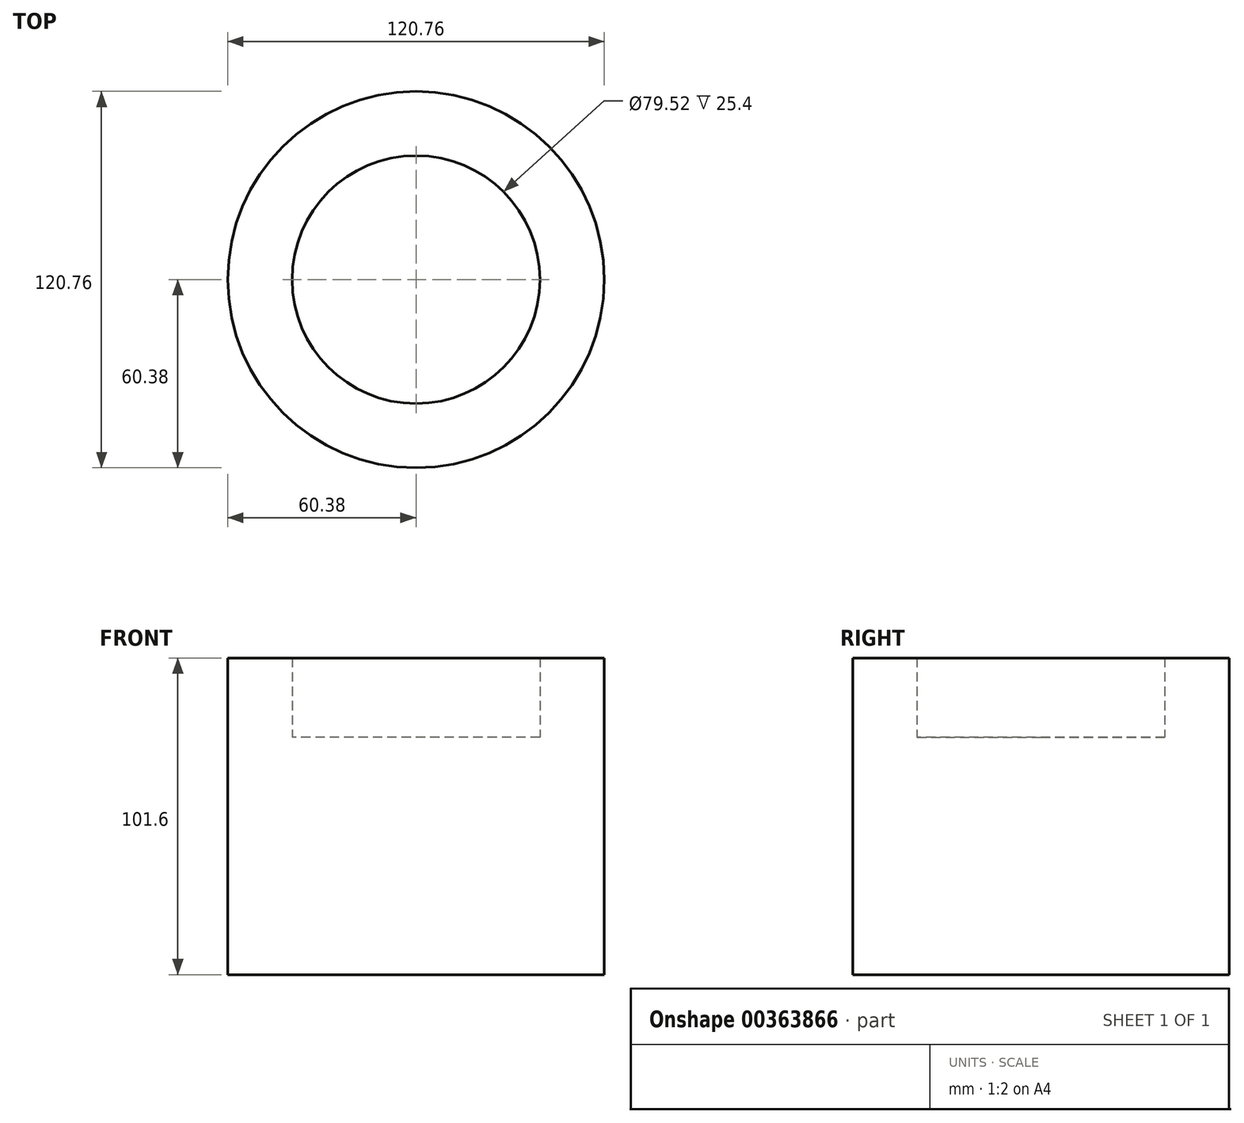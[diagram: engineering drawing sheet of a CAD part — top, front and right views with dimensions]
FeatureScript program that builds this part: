
annotation { "Feature Type Name" : "Feature", "Feature Type Description" : "" }
export const myFeature = defineFeature(function(context is Context, id is Id, definition is map)
    precondition{}
    {
        {
            var Q0;
            Q0=qCreatedBy(makeId("Top.planeOp"),FACE);
            var sketch = newSketch(context, id + "F0", { "sketchPlane" : qUnion([Q0])});
            skCircle(sketch, "E0", {"center": v(0, 0) * mm, "radius": 60.38 * mm});
            skSolve(sketch);
        }
        {
            var Q0;
            Q0=makeQuery(id+"F0.imprint","IMPRINT",FACE,{"disambiguationData":[TD([[makeQuery(id+"F0.imprint","IMPRINT",EDGE,{"derivedFrom":sQuery(id+"F0.wireOp",EDGE,"E0")}),1.0]])]});
            extrude(context, id + "F1", {"entities" : qUnion([Q0]), "endBound" : BoundingType.SYMMETRIC, "depth" : 76.2 * mm});
        }
        {
            var Q0;
            Q0=makeQuery(id+"F1.opExtrude","CAP_FACE",FACE,{"disambiguationData":[OSD([sQuery(id+"F0.wireOp",EDGE,"E0")])],"isStart":false});
            var sketch = newSketch(context, id + "F2", { "sketchPlane" : qUnion([Q0])});
            skCircle(sketch, "E1", {"center": v(0, 0) * mm, "radius": 39.76 * mm});
            skSolve(sketch);
        }
        {
            var Q0;
            Q0=makeQuery(id+"F2.imprint","IMPRINT",FACE,{"disambiguationData":[TD([[makeQuery(id+"F2.imprint","IMPRINT",EDGE,{"derivedFrom":sQuery(id+"F2.wireOp",EDGE,"E1")}),-1.0]])]});
            extrude(context, id + "F3", {"entities" : qUnion([Q0]), "operationType" : NewBodyOperationType.ADD, "depth" : 25.4 * mm});
        }
    });
